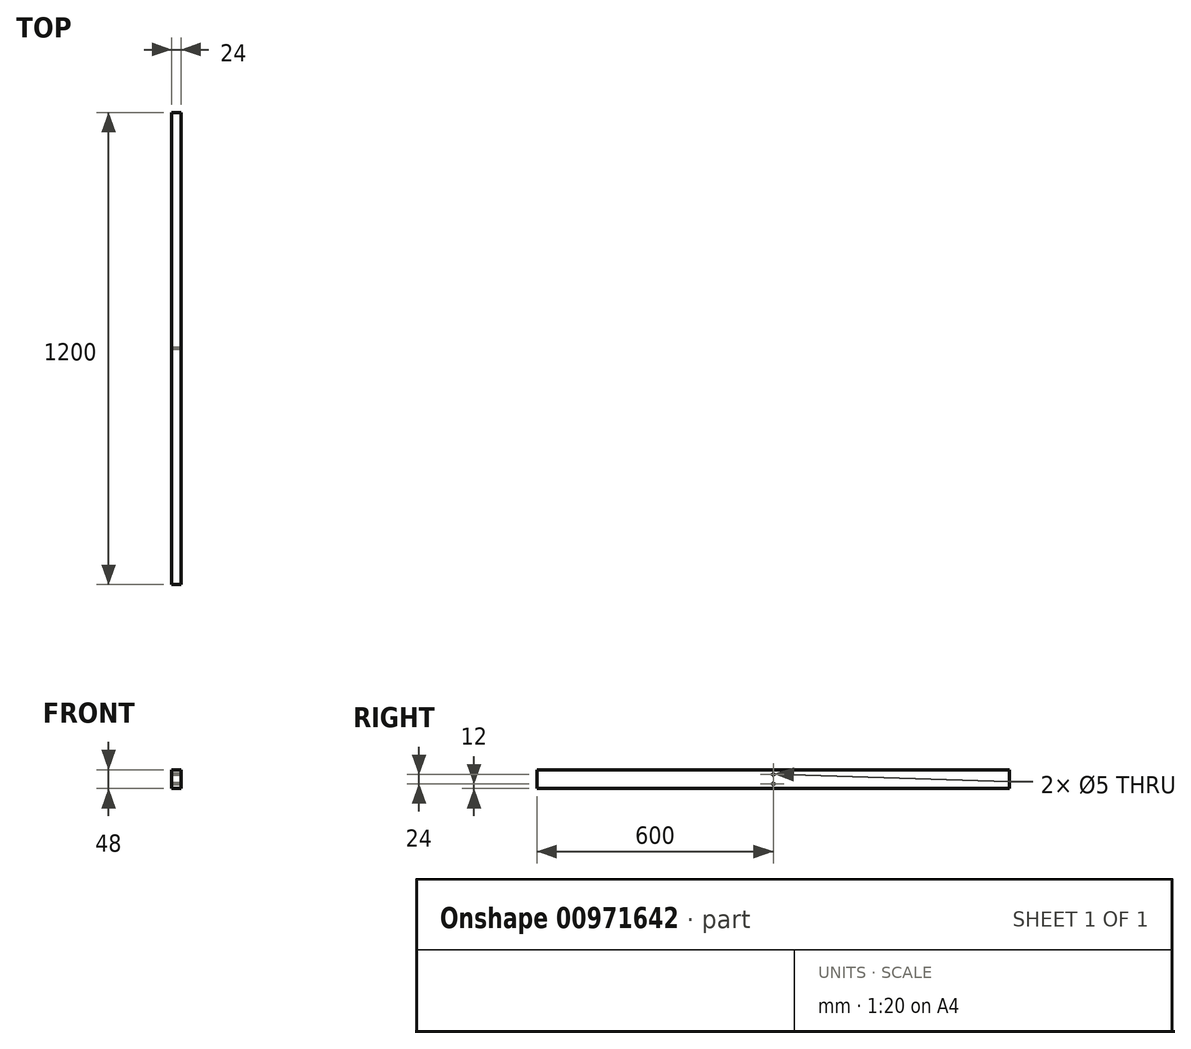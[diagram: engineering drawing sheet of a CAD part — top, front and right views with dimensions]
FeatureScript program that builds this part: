
annotation { "Feature Type Name" : "Feature", "Feature Type Description" : "" }
export const myFeature = defineFeature(function(context is Context, id is Id, definition is map)
    precondition{}
    {
        {
            assignVariable(context, id + "F0", {"name" : "c", "anyValue" : 1200});
        }
        {
            assignVariable(context, id + "F1", {"name" : "a", "anyValue" : 24});
        }
        {
            var Q0;
            Q0=qCreatedBy(makeId("Front.planeOp"),FACE);
            var sketch = newSketch(context, id + "F2", { "sketchPlane" : qUnion([Q0])});
            skLineSegment(sketch, "E0.bottom", {"start": v(12, -24) * mm, "end": v(-12, -24) * mm});
            skLineSegment(sketch, "E0.top", {"start": v(12, 24) * mm, "end": v(-12, 24) * mm});
            skLineSegment(sketch, "E0.left", {"start": v(12, -24) * mm, "end": v(12, 24) * mm});
            skLineSegment(sketch, "E0.right", {"start": v(-12, -24) * mm, "end": v(-12, 24) * mm});
            skPoint(sketch, "E0.middle", {"position": v(0, 0) * mm});
            skSolve(sketch);
        }
        {
            var Q0;
            Q0=qSketchRegion(id+"F2",true);
            var Q1;
            Q1=makeQuery(id+"F2.imprint","IMPRINT",FACE,{"disambiguationData":[TD([[makeQuery(id+"F2.imprint","IMPRINT",EDGE,{"derivedFrom":sQuery(id+"F2.wireOp",EDGE,"E0.bottom")}),-1.0]])]});
            extrude(context, id + "F3", {"entities" : qUnion([Q0, Q1]), "depth" : (getVariable(context, 'c')) * mm, "offsetDistance" : 25 * mm});
        }
        {
            var Q0;
            Q0=makeQuery(id+"F3.opExtrude","SWEPT_FACE",FACE,{"disambiguationData":[OSD([sQuery(id+"F2.wireOp",EDGE,"E0.right")])]});
            var sketch = newSketch(context, id + "F4", { "sketchPlane" : qUnion([Q0])});
            skLineSegment(sketch, "E1", {"start": v(0, 0) * mm, "end": v(600, 0) * mm});
            skLineSegment(sketch, "E2", {"start": v(600, 0) * mm, "end": v(1400, 0) * mm});
            skLineSegment(sketch, "E3", {"start": v(600, 0) * mm, "end": v(600, 12) * mm});
            skLineSegment(sketch, "E4", {"start": v(600, 0) * mm, "end": v(600, -12) * mm});
            skCircle(sketch, "E5", {"center": v(600, 12) * mm, "radius": 2.5 * mm});
            skCircle(sketch, "E6", {"center": v(600, -12) * mm, "radius": 2.5 * mm});
            skLineSegment(sketch, "E7", {"start": v(1400, 0) * mm, "end": v(1400, 12) * mm});
            skLineSegment(sketch, "E8", {"start": v(1400, 0) * mm, "end": v(1400, -12) * mm});
            skCircle(sketch, "E9", {"center": v(1400, 12) * mm, "radius": 2.5 * mm});
            skCircle(sketch, "E10", {"center": v(1400, -12) * mm, "radius": 2.5 * mm});
            skSolve(sketch);
        }
        {
            var Q0;
            Q0=makeQuery(id+"F4.imprint","IMPRINT",FACE,{"disambiguationData":[TD([[makeQuery(id+"F4.imprint","IMPRINT",EDGE,{"derivedFrom":sQuery(id+"F4.wireOp",EDGE,"E9")}),1.0]])]});
            var Q1;
            Q1=makeQuery(id+"F4.imprint","IMPRINT",FACE,{"disambiguationData":[TD([[makeQuery(id+"F4.imprint","IMPRINT",EDGE,{"derivedFrom":sQuery(id+"F4.wireOp",EDGE,"E10")}),1.0]])]});
            var Q2;
            Q2=makeQuery(id+"F4.imprint","IMPRINT",FACE,{"disambiguationData":[TD([[makeQuery(id+"F4.imprint","IMPRINT",EDGE,{"derivedFrom":sQuery(id+"F4.wireOp",EDGE,"E6")}),1.0]])]});
            var Q3;
            Q3=makeQuery(id+"F4.imprint","IMPRINT",FACE,{"disambiguationData":[TD([[makeQuery(id+"F4.imprint","IMPRINT",EDGE,{"derivedFrom":sQuery(id+"F4.wireOp",EDGE,"E5")}),1.0]])]});
            extrude(context, id + "F5", {"entities" : qUnion([Q0, Q1, Q2, Q3]), "operationType" : NewBodyOperationType.REMOVE, "oppositeDirection" : true, "depth" : (getVariable(context, 'a')) * mm, "offsetDistance" : 25 * mm});
        }
    });
